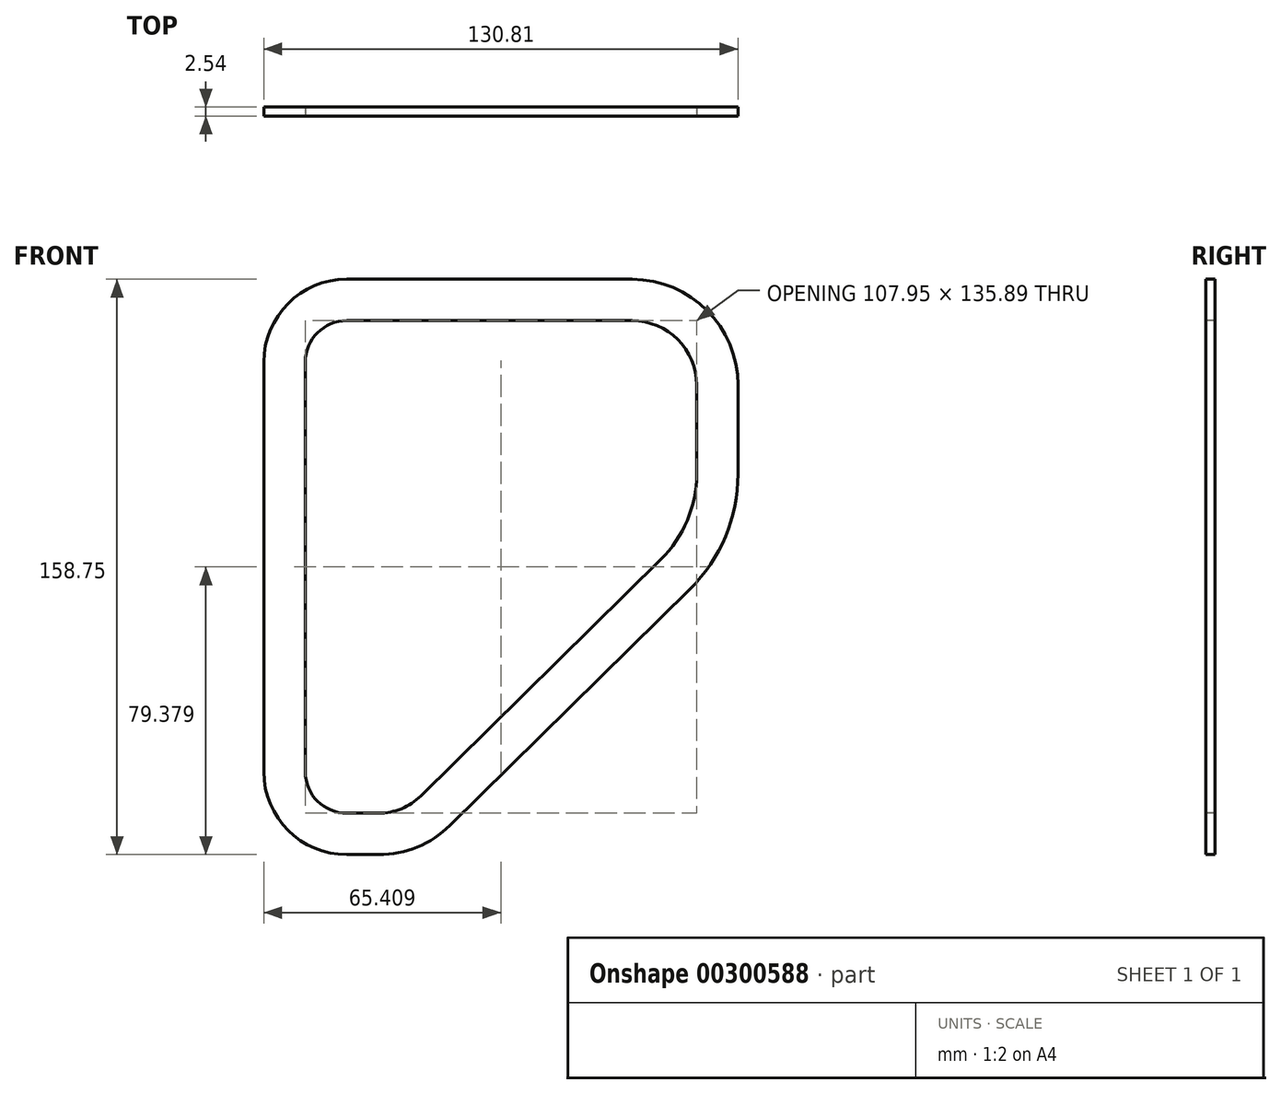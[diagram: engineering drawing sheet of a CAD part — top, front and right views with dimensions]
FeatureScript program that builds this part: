
annotation { "Feature Type Name" : "Feature", "Feature Type Description" : "" }
export const myFeature = defineFeature(function(context is Context, id is Id, definition is map)
    precondition{}
    {
        {
            var Q0;
            Q0=qCreatedBy(makeId("Front.planeOp"),FACE);
            var sketch = newSketch(context, id + "F0", { "sketchPlane" : qUnion([Q0])});
            skLineSegment(sketch, "E0", {"start": v(-66.65, 70.27) * mm, "end": v(-66.65, -88.48) * mm});
            skLineSegment(sketch, "E1", {"start": v(-66.65, -88.48) * mm, "end": v(-23.47, -88.48) * mm});
            skLineSegment(sketch, "E2", {"start": v(-23.47, -88.48) * mm, "end": v(64.16, -2.12) * mm});
            skLineSegment(sketch, "E3", {"start": v(64.16, -2.12) * mm, "end": v(64.16, 70.27) * mm});
            skLineSegment(sketch, "E4", {"start": v(64.16, 70.27) * mm, "end": v(-66.65, 70.27) * mm});
            skSolve(sketch);
        }
        {
            var Q0;
            Q0=makeQuery(id+"F0.imprint","IMPRINT",FACE,{"disambiguationData":[TD([[makeQuery(id+"F0.imprint","IMPRINT",EDGE,{"derivedFrom":sQuery(id+"F0.wireOp",EDGE,"E0")}),1.0]])]});
            extrude(context, id + "F1", {"entities" : qUnion([Q0]), "depth" : 2.54 * mm});
        }
        {
            var Q0;
            Q0=makeQuery(id+"F1.opExtrude","SWEPT_EDGE",EDGE,{"disambiguationData":[OSD([sQuery(id+"F0.wireOp",EDGE,"E0"),sQuery(id+"F0.wireOp",EDGE,"E4")])]});
            fillet(context, id + "F2", {"entities" : qUnion([Q0]), "radius" : 22.86 * mm, "tangentPropagation" : true, "allowEdgeOverflow" : false});
        }
        {
            var Q0;
            Q0=makeQuery(id+"F1.opExtrude","SWEPT_EDGE",EDGE,{"disambiguationData":[OSD([sQuery(id+"F0.wireOp",EDGE,"E3"),sQuery(id+"F0.wireOp",EDGE,"E4")])]});
            fillet(context, id + "F3", {"entities" : qUnion([Q0]), "radius" : 29.2 * mm, "tangentPropagation" : true, "allowEdgeOverflow" : false});
        }
        {
            var Q0;
            Q0=makeQuery(id+"F1.opExtrude","SWEPT_EDGE",EDGE,{"disambiguationData":[OSD([sQuery(id+"F0.wireOp",EDGE,"E2"),sQuery(id+"F0.wireOp",EDGE,"E3")])]});
            fillet(context, id + "F4", {"entities" : qUnion([Q0]), "radius" : 44.45 * mm, "tangentPropagation" : true, "allowEdgeOverflow" : false});
        }
        {
            var Q0;
            Q0=makeQuery(id+"F1.opExtrude","SWEPT_EDGE",EDGE,{"disambiguationData":[OSD([sQuery(id+"F0.wireOp",EDGE,"E0"),sQuery(id+"F0.wireOp",EDGE,"E1")])]});
            fillet(context, id + "F5", {"entities" : qUnion([Q0]), "radius" : 22.86 * mm, "tangentPropagation" : true, "allowEdgeOverflow" : false});
        }
        {
            var Q0;
            Q0=makeQuery(id+"F1.opExtrude","SWEPT_EDGE",EDGE,{"disambiguationData":[OSD([sQuery(id+"F0.wireOp",EDGE,"E1"),sQuery(id+"F0.wireOp",EDGE,"E2")])]});
            fillet(context, id + "F6", {"entities" : qUnion([Q0]), "radius" : 27.94 * mm, "tangentPropagation" : true, "allowEdgeOverflow" : false});
        }
        {
            var Q0;
            Q0=makeQuery(id+"F1.opExtrude","CAP_FACE",FACE,{"disambiguationData":[OSD([sQuery(id+"F0.wireOp",EDGE,"E0"),sQuery(id+"F0.wireOp",EDGE,"E1"),sQuery(id+"F0.wireOp",EDGE,"E2"),sQuery(id+"F0.wireOp",EDGE,"E3"),sQuery(id+"F0.wireOp",EDGE,"E4")])],"isStart":false});
            var sketch = newSketch(context, id + "F7", { "sketchPlane" : qUnion([Q0])});
            skLineSegment(sketch, "E5.0.0", {"start": v(-43.79, -88.48) * mm, "end": v(-34.92, -88.48) * mm, "construction": true});
            skArc(sketch, "E5.0.1", {"start": v(-34.92, -88.48) * mm, "mid": v(-24.32, -86.39) * mm, "end": v(-15.3, -80.44) * mm, "construction": true});
            skLineSegment(sketch, "E5.0.2", {"start": v(-15.3, -80.44) * mm, "end": v(50.92, -15.17) * mm, "construction": true});
            skArc(sketch, "E5.0.3", {"start": v(50.92, -15.17) * mm, "mid": v(60.72, -0.67) * mm, "end": v(64.16, 16.49) * mm, "construction": true});
            skLineSegment(sketch, "E5.0.4", {"start": v(64.16, 16.49) * mm, "end": v(64.16, 41.06) * mm, "construction": true});
            skArc(sketch, "E5.0.5", {"start": v(64.16, 41.06) * mm, "mid": v(55.6, 61.72) * mm, "end": v(34.95, 70.27) * mm, "construction": true});
            skLineSegment(sketch, "E5.0.6", {"start": v(34.95, 70.27) * mm, "end": v(-43.79, 70.27) * mm, "construction": true});
            skArc(sketch, "E5.0.7", {"start": v(-43.79, 70.27) * mm, "mid": v(-59.95, 63.58) * mm, "end": v(-66.65, 47.41) * mm, "construction": true});
            skLineSegment(sketch, "E5.0.8", {"start": v(-66.65, 47.41) * mm, "end": v(-66.65, -65.62) * mm, "construction": true});
            skArc(sketch, "E5.0.9", {"start": v(-66.65, -65.62) * mm, "mid": v(-59.95, -81.78) * mm, "end": v(-43.79, -88.48) * mm, "construction": true});
            skLineSegment(sketch, "E6.0", {"start": v(52.73, 16.49) * mm, "end": v(52.73, 41.06) * mm});
            skArc(sketch, "E6.1", {"start": v(42.9, -7.03) * mm, "mid": v(50.17, 3.74) * mm, "end": v(52.73, 16.49) * mm});
            skArc(sketch, "E6.2", {"start": v(52.73, 41.06) * mm, "mid": v(47.53, 53.64) * mm, "end": v(34.95, 58.84) * mm});
            skLineSegment(sketch, "E6.3", {"start": v(-23.33, -72.3) * mm, "end": v(42.9, -7.03) * mm});
            skArc(sketch, "E6.4", {"start": v(-34.92, -77.05) * mm, "mid": v(-28.66, -75.81) * mm, "end": v(-23.33, -72.3) * mm});
            skLineSegment(sketch, "E6.5", {"start": v(-43.79, -77.05) * mm, "end": v(-34.92, -77.05) * mm});
            skLineSegment(sketch, "E6.6", {"start": v(34.95, 58.84) * mm, "end": v(-43.79, 58.84) * mm});
            skArc(sketch, "E6.7", {"start": v(-43.79, 58.84) * mm, "mid": v(-51.87, 55.5) * mm, "end": v(-55.22, 47.41) * mm});
            skLineSegment(sketch, "E6.8", {"start": v(-55.22, 47.41) * mm, "end": v(-55.22, -65.62) * mm});
            skArc(sketch, "E6.9", {"start": v(-55.22, -65.62) * mm, "mid": v(-51.87, -73.7) * mm, "end": v(-43.79, -77.05) * mm});
            skArc(sketch, "E7.0", {"start": v(-73, -65.62) * mm, "mid": v(-64.44, -86.27) * mm, "end": v(-43.79, -94.83) * mm, "construction": true});
            skLineSegment(sketch, "E7.1", {"start": v(-73, 47.41) * mm, "end": v(-73, -65.62) * mm, "construction": true});
            skLineSegment(sketch, "E7.2", {"start": v(-43.79, -94.83) * mm, "end": v(-34.55, -94.83) * mm, "construction": true});
            skArc(sketch, "E7.3", {"start": v(-43.79, 76.62) * mm, "mid": v(-64.44, 68.07) * mm, "end": v(-73, 47.41) * mm, "construction": true});
            skLineSegment(sketch, "E7.4", {"start": v(34.95, 76.62) * mm, "end": v(-43.79, 76.62) * mm, "construction": true});
            skArc(sketch, "E7.5", {"start": v(70.51, 41.06) * mm, "mid": v(60.1, 66.2) * mm, "end": v(34.95, 76.62) * mm, "construction": true});
            skArc(sketch, "E7.6", {"start": v(-34.55, -94.83) * mm, "mid": v(-21.9, -92.4) * mm, "end": v(-11.04, -85.5) * mm, "construction": true});
            skLineSegment(sketch, "E7.7", {"start": v(-11.04, -85.5) * mm, "end": v(57.74, -20.7) * mm, "construction": true});
            skArc(sketch, "E7.8", {"start": v(57.74, -20.7) * mm, "mid": v(67.18, -7.23) * mm, "end": v(70.51, 8.88) * mm, "construction": true});
            skLineSegment(sketch, "E7.9", {"start": v(70.51, 8.88) * mm, "end": v(70.51, 41.06) * mm, "construction": true});
            skSolve(sketch);
        }
        {
            var Q0;
            Q0 = qSketchRegion(id + "F7", true);
            var Q1;
            Q1 = qConstructionFilter(qBodyType(qCreatedBy(id + "F7" ,EDGE), BodyType.WIRE), ConstructionObject.NO);
            extrude(context, id + "F8", {"entities" : qUnion([Q0]), "operationType" : NewBodyOperationType.REMOVE, "surfaceEntities" : qUnion([Q1]), "endBound" : BoundingType.UP_TO_NEXT, "oppositeDirection" : true, "depth" : 25.4 * mm});
        }
    });
